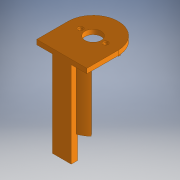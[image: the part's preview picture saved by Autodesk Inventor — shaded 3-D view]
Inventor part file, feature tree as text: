
AUTODESK INVENTOR PART (.ipt)
format: ipt  version: 2018 (Build 220112000, 112)  size: 167,424 bytes
history: native  units: mm
features: sketch x5, extrude x5, other x2, hole x1, chamfer x1, reference x1
ambient origin geometry x8: Origin, YZ Plane, XZ Plane, XY Plane, X Axis, Y Axis, Z Axis, Center Point
bodies: Solid1 (feature_tree)
feature tree (15):
  sketch  "Sketch1"  dims[d0=10.3mm d1=32.0mm]
  extrude  "Extrusion1"  Depth=32.0mm
  hole  "Hole1"  [1 undecoded]
  extrude  "Extrusion2"  Depth=3.0mm TaperAngle=0.0deg
  extrude  "Extrusion3"  Depth=3.0mm
  chamfer  "Chamfer1"  Distance=15.0mm
  extrude  "Extrusion4"  Depth=3.0mm
  extrude  "Extrusion5"  Depth=12.0mm
  sketch  "Sketch2"  dims[d3=20.0mm d4=8.0mm]
  sketch  "Sketch3"  dims[d5=8.0mm d6=3.0mm d7=0.0mm]
  reference  "Reference1"
  sketch  "Sketch4"  dims[d8=2.3mm d9=6.0mm d10=4.0mm d11=2.0mm d12=90.0deg d13=8.0mm d14=20.594885mm d15=3.0mm]
  sketch  "Sketch6"  dims[d16=1.25mm d17=15.0mm d18=0.0mm d19=3.0mm d20=12.0mm d21=24.0mm d22=12.0mm d23=40.0mm d24=0.0mm d25=0.5mm d26=2.0mm d27=45.0deg d28=1.5mm d29=4.0mm d30=18.0mm d31=0.0mm d36=2.3mm d37=9.3mm d38=6.0mm d39=0.0mm]
  other  "Default Motor Testbench Mk2.iam"
  other  "JD5B-2655W-R:1"
note: 1 required parameter value undecoded (feature->parameter linkage not recoverable at this tier; creation-order binding heuristic only, values carry confidence <= 0.55)
